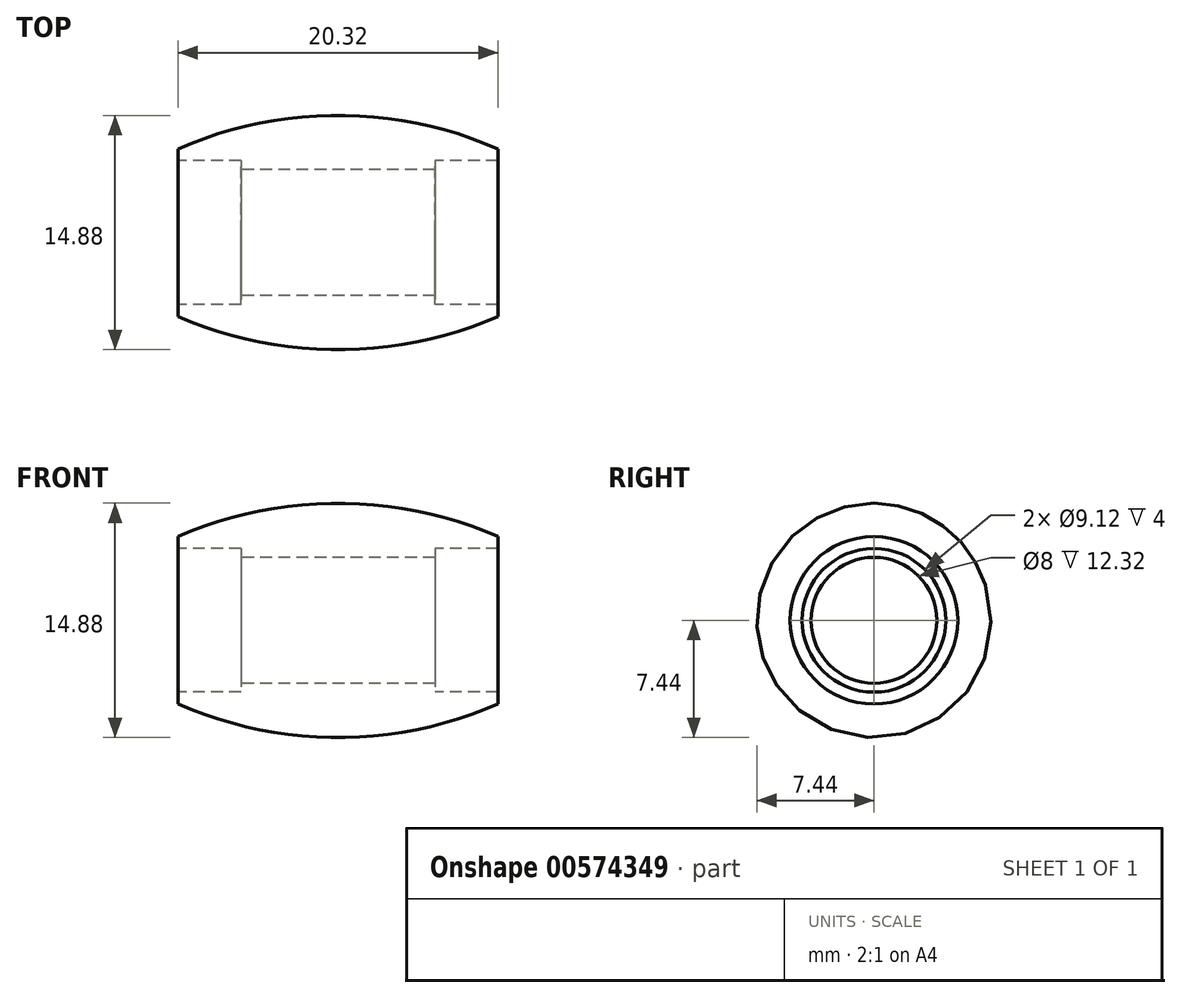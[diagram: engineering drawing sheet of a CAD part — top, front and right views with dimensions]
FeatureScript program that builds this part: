
annotation { "Feature Type Name" : "Feature", "Feature Type Description" : "" }
export const myFeature = defineFeature(function(context is Context, id is Id, definition is map)
    precondition{}
    {
        {
            var Q0;
            Q0=qCreatedBy(makeId("Front.planeOp"),FACE);
            var sketch = newSketch(context, id + "F0", { "sketchPlane" : qUnion([Q0])});
            skCircle(sketch, "E0", {"center": v(0, -17.96) * mm, "radius": 25.4 * mm, "construction": true});
            skLineSegment(sketch, "E1", {"start": v(-17.96, 0) * mm, "end": v(17.96, 0) * mm, "construction": true});
            skLineSegment(sketch, "E2", {"start": v(17.96, 0) * mm, "end": v(0, -17.96) * mm, "construction": true});
            skLineSegment(sketch, "E3", {"start": v(0, -17.96) * mm, "end": v(-17.96, 0) * mm, "construction": true});
            skLineSegment(sketch, "E4", {"start": v(-10.16, 4.56) * mm, "end": v(-6.16, 4.56) * mm});
            skLineSegment(sketch, "E5", {"start": v(-6.16, 4.56) * mm, "end": v(-6.16, 4) * mm});
            skLineSegment(sketch, "E6", {"start": v(-6.16, 4) * mm, "end": v(6.16, 4) * mm});
            skLineSegment(sketch, "E7", {"start": v(6.16, 4) * mm, "end": v(6.16, 4.56) * mm});
            skLineSegment(sketch, "E8", {"start": v(6.16, 4.56) * mm, "end": v(10.16, 4.56) * mm});
            skLineSegment(sketch, "E9", {"start": v(10.16, 4.56) * mm, "end": v(10.16, 5.32) * mm});
            skLineSegment(sketch, "E10", {"start": v(-10.16, 4.56) * mm, "end": v(-10.16, 5.32) * mm});
            skArc(sketch, "E11", {"start": v(-10.16, 5.32) * mm, "mid": v(0, 7.44) * mm, "end": v(10.16, 5.32) * mm});
            skSolve(sketch);
        }
        {
            var Q0;
            Q0 = qSketchRegion(id + "F0", true);
            var Q1;
            Q1=sQuery(id+"F0.wireOp",EDGE,"E1");
            revolve(context, id + "F1", {"entities" : qUnion([Q0]), "axis" : qUnion([Q1]), "revolveType" : RevolveType.FULL});
        }
    });
